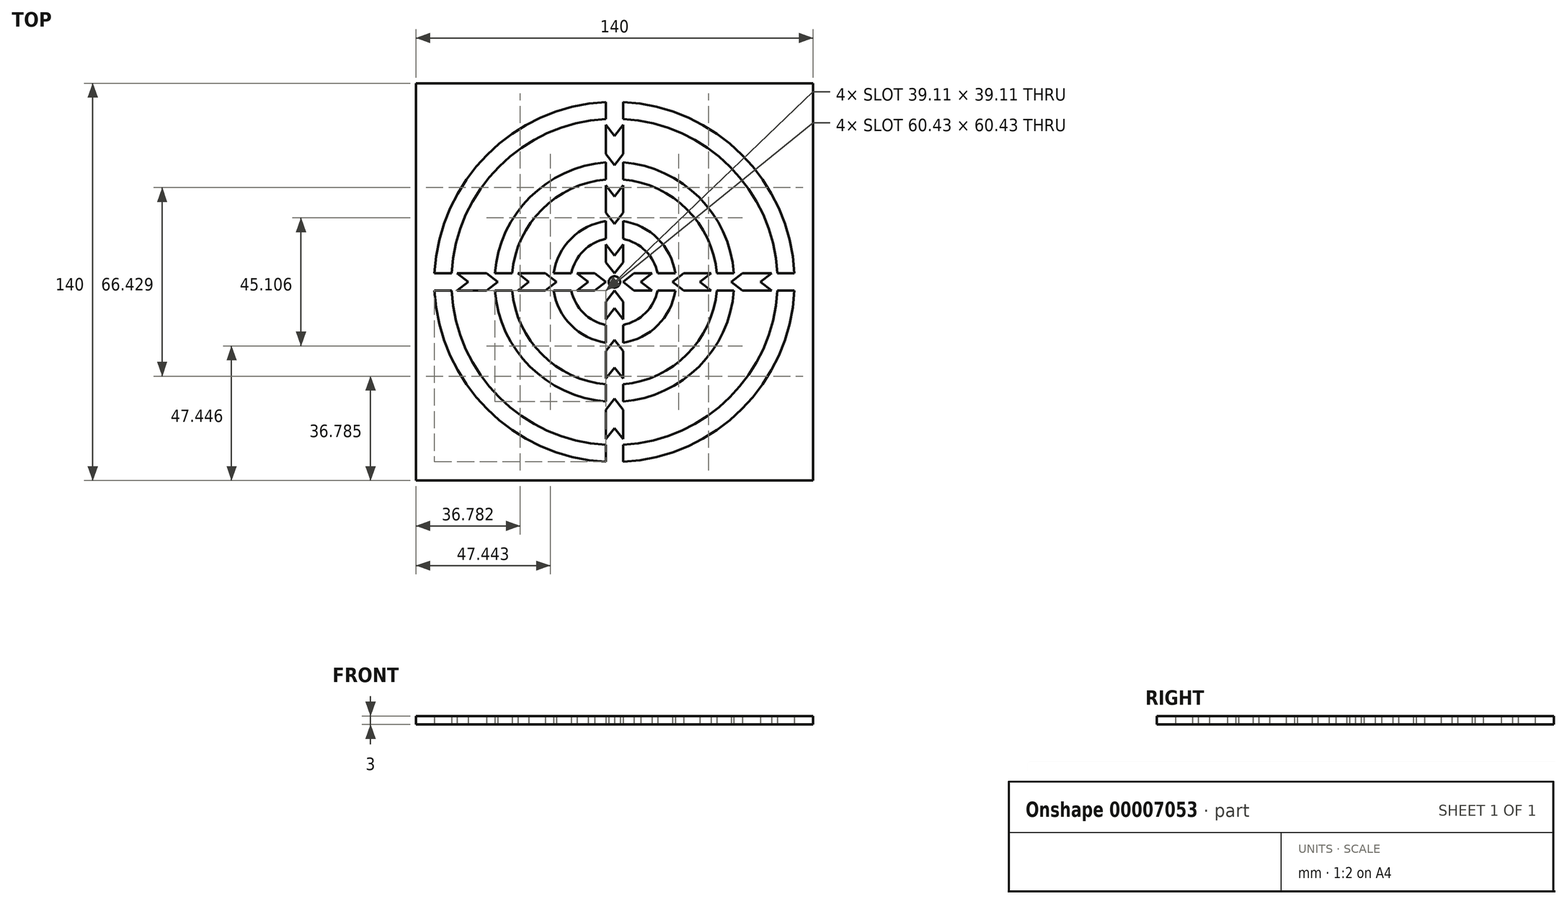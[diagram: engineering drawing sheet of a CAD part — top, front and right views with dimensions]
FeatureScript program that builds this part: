
annotation { "Feature Type Name" : "Feature", "Feature Type Description" : "" }
export const myFeature = defineFeature(function(context is Context, id is Id, definition is map)
    precondition{}
    {
        {
            var Q0;
            Q0=qCreatedBy(makeId("Top.planeOp"),FACE);
            var sketch = newSketch(context, id + "F0", { "sketchPlane" : qUnion([Q0])});
            skLineSegment(sketch, "E0.bottom", {"start": v(-138.4, 77.9) * mm, "end": v(1.6, 77.9) * mm});
            skLineSegment(sketch, "E0.top", {"start": v(-138.4, -62.1) * mm, "end": v(1.6, -62.1) * mm});
            skLineSegment(sketch, "E0.left", {"start": v(-138.4, 77.9) * mm, "end": v(-138.4, -62.1) * mm});
            skLineSegment(sketch, "E0.right", {"start": v(1.6, 77.9) * mm, "end": v(1.6, -62.1) * mm});
            skLineSegment(sketch, "E1", {"start": v(-138.4, 77.9) * mm, "end": v(1.6, -62.1) * mm, "construction": true});
            skLineSegment(sketch, "E2", {"start": v(1.6, 77.9) * mm, "end": v(-138.4, -62.1) * mm, "construction": true});
            skLineSegment(sketch, "E3", {"start": v(-68.4, 7.9) * mm, "end": v(-68.4, 77.9) * mm, "construction": true});
            skLineSegment(sketch, "E4", {"start": v(-68.4, 77.9) * mm, "end": v(-68.4, 7.9) * mm, "construction": true});
            skLineSegment(sketch, "E5", {"start": v(-68.4, 7.9) * mm, "end": v(1.6, 7.9) * mm, "construction": true});
            skLineSegment(sketch, "E6", {"start": v(1.6, 10.9) * mm, "end": v(-138.4, 10.9) * mm, "construction": true});
            skLineSegment(sketch, "E7", {"start": v(1.6, 4.9) * mm, "end": v(-138.4, 4.9) * mm, "construction": true});
            skLineSegment(sketch, "E8", {"start": v(-71.4, 77.9) * mm, "end": v(-71.4, -62.1) * mm, "construction": true});
            skLineSegment(sketch, "E9", {"start": v(-65.4, 77.9) * mm, "end": v(-65.4, -62.1) * mm, "construction": true});
            skLineSegment(sketch, "E10", {"start": v(-71.4, 71.33) * mm, "end": v(-71.4, 65.32) * mm});
            skLineSegment(sketch, "E11", {"start": v(-131.82, 10.9) * mm, "end": v(-125.82, 10.9) * mm});
            skArc(sketch, "E12", {"start": v(-71.4, 71.33) * mm, "mid": v(-113.26, 52.77) * mm, "end": v(-131.82, 10.9) * mm});
            skArc(sketch, "E13", {"start": v(-71.4, 65.32) * mm, "mid": v(-109.05, 48.55) * mm, "end": v(-125.82, 10.9) * mm});
            skArc(sketch, "E14", {"start": v(-71.4, 50) * mm, "mid": v(-98.21, 37.72) * mm, "end": v(-110.5, 10.9) * mm});
            skArc(sketch, "E15", {"start": v(-71.4, 43.99) * mm, "mid": v(-93.97, 33.48) * mm, "end": v(-104.48, 10.9) * mm});
            skLineSegment(sketch, "E16", {"start": v(-110.5, 10.9) * mm, "end": v(-104.48, 10.9) * mm});
            skLineSegment(sketch, "E17", {"start": v(-71.4, 50) * mm, "end": v(-71.4, 43.99) * mm});
            skLineSegment(sketch, "E18", {"start": v(-71.4, 29.31) * mm, "end": v(-71.4, 23.09) * mm});
            skLineSegment(sketch, "E19", {"start": v(-89.8, 10.9) * mm, "end": v(-83.58, 10.9) * mm});
            skArc(sketch, "E20", {"start": v(-71.4, 29.31) * mm, "mid": v(-83.68, 23.18) * mm, "end": v(-89.8, 10.9) * mm});
            skArc(sketch, "E21", {"start": v(-71.4, 23.09) * mm, "mid": v(-79.32, 18.83) * mm, "end": v(-83.58, 10.9) * mm});
            skLineSegment(sketch, "E22", {"start": v(-71.4, 63.32) * mm, "end": v(-68.4, 59.4) * mm});
            skLineSegment(sketch, "E23", {"start": v(-71.4, 53) * mm, "end": v(-68.4, 49.08) * mm});
            skLineSegment(sketch, "E24", {"start": v(-71.4, 32.31) * mm, "end": v(-68.4, 28.4) * mm});
            skLineSegment(sketch, "E25", {"start": v(-71.4, 21.09) * mm, "end": v(-68.4, 17.17) * mm});
            skLineSegment(sketch, "E26", {"start": v(-71.4, 14.82) * mm, "end": v(-68.4, 10.9) * mm});
            skLineSegment(sketch, "E27", {"start": v(-71.4, 41.99) * mm, "end": v(-68.4, 38.06) * mm});
            skLineSegment(sketch, "E28.MirrorCS", {"start": v(-123.82, 10.9) * mm, "end": v(-119.9, 7.9) * mm});
            skLineSegment(sketch, "E29.MirrorCS", {"start": v(-113.5, 10.9) * mm, "end": v(-109.58, 7.9) * mm});
            skLineSegment(sketch, "E30.MirrorCS", {"start": v(-102.48, 10.9) * mm, "end": v(-98.56, 7.9) * mm});
            skLineSegment(sketch, "E31.MirrorCS", {"start": v(-92.8, 10.9) * mm, "end": v(-88.89, 7.9) * mm});
            skLineSegment(sketch, "E32.MirrorCS", {"start": v(-75.32, 10.9) * mm, "end": v(-71.4, 7.9) * mm});
            skLineSegment(sketch, "E33.MirrorCS", {"start": v(-81.58, 10.9) * mm, "end": v(-77.66, 7.9) * mm});
            skLineSegment(sketch, "E34", {"start": v(-71.4, 63.32) * mm, "end": v(-71.4, 53) * mm});
            skLineSegment(sketch, "E35", {"start": v(-71.4, 41.99) * mm, "end": v(-71.4, 32.31) * mm});
            skLineSegment(sketch, "E36", {"start": v(-71.4, 21.09) * mm, "end": v(-71.4, 14.82) * mm});
            skLineSegment(sketch, "E37.MirrorCS", {"start": v(-123.82, 10.9) * mm, "end": v(-113.5, 10.9) * mm});
            skLineSegment(sketch, "E38.MirrorCS", {"start": v(-81.58, 10.9) * mm, "end": v(-75.32, 10.9) * mm});
            skLineSegment(sketch, "E39.MirrorCS", {"start": v(-102.48, 10.9) * mm, "end": v(-92.8, 10.9) * mm});
            skLineSegment(sketch, "E40.MirrorCS", {"start": v(-61.47, 10.9) * mm, "end": v(-65.4, 7.9) * mm});
            skLineSegment(sketch, "E41.MirrorCS", {"start": v(-55.2, 10.9) * mm, "end": v(-61.47, 10.9) * mm});
            skLineSegment(sketch, "E42.MirrorCS", {"start": v(-55.2, 10.9) * mm, "end": v(-59.12, 7.9) * mm});
            skLineSegment(sketch, "E43.MirrorCS", {"start": v(-46.98, 10.9) * mm, "end": v(-53.2, 10.9) * mm});
            skLineSegment(sketch, "E44.MirrorCS", {"start": v(-43.98, 10.9) * mm, "end": v(-47.9, 7.9) * mm});
            skLineSegment(sketch, "E45.MirrorCS", {"start": v(-34.3, 10.9) * mm, "end": v(-43.98, 10.9) * mm});
            skLineSegment(sketch, "E46.MirrorCS", {"start": v(-34.3, 10.9) * mm, "end": v(-38.23, 7.9) * mm});
            skLineSegment(sketch, "E47.MirrorCS", {"start": v(-26.29, 10.9) * mm, "end": v(-32.3, 10.9) * mm});
            skLineSegment(sketch, "E48.MirrorCS", {"start": v(-23.29, 10.9) * mm, "end": v(-27.2, 7.9) * mm});
            skLineSegment(sketch, "E49.MirrorCS", {"start": v(-12.97, 10.9) * mm, "end": v(-16.9, 7.9) * mm});
            skLineSegment(sketch, "E50.MirrorCS", {"start": v(-12.97, 10.9) * mm, "end": v(-23.29, 10.9) * mm});
            skLineSegment(sketch, "E51.MirrorCS", {"start": v(-4.96, 10.9) * mm, "end": v(-10.97, 10.9) * mm});
            skLineSegment(sketch, "E52.MirrorCS", {"start": v(-65.4, 14.82) * mm, "end": v(-68.4, 10.9) * mm});
            skArc(sketch, "E53.MirrorCS", {"start": v(-65.4, 23.09) * mm, "mid": v(-57.47, 18.83) * mm, "end": v(-53.2, 10.9) * mm});
            skLineSegment(sketch, "E54.MirrorCS", {"start": v(-65.4, 21.09) * mm, "end": v(-68.4, 17.17) * mm});
            skLineSegment(sketch, "E55.MirrorCS", {"start": v(-65.4, 29.31) * mm, "end": v(-65.4, 23.09) * mm});
            skArc(sketch, "E56.MirrorCS", {"start": v(-65.4, 29.31) * mm, "mid": v(-53.1, 23.18) * mm, "end": v(-46.98, 10.9) * mm});
            skLineSegment(sketch, "E57.MirrorCS", {"start": v(-65.4, 32.31) * mm, "end": v(-68.4, 28.4) * mm});
            skLineSegment(sketch, "E58.MirrorCS", {"start": v(-65.4, 41.99) * mm, "end": v(-68.4, 38.06) * mm});
            skLineSegment(sketch, "E59.MirrorCS", {"start": v(-65.4, 41.99) * mm, "end": v(-65.4, 32.31) * mm});
            skArc(sketch, "E60.MirrorCS", {"start": v(-65.4, 43.99) * mm, "mid": v(-42.82, 33.48) * mm, "end": v(-32.3, 10.9) * mm});
            skLineSegment(sketch, "E61.MirrorCS", {"start": v(-65.4, 50) * mm, "end": v(-65.4, 43.99) * mm});
            skArc(sketch, "E62.MirrorCS", {"start": v(-65.4, 50) * mm, "mid": v(-38.58, 37.72) * mm, "end": v(-26.29, 10.9) * mm});
            skLineSegment(sketch, "E63.MirrorCS", {"start": v(-65.4, 53) * mm, "end": v(-68.4, 49.08) * mm});
            skLineSegment(sketch, "E64.MirrorCS", {"start": v(-65.4, 63.32) * mm, "end": v(-65.4, 53) * mm});
            skLineSegment(sketch, "E65.MirrorCS", {"start": v(-65.4, 71.33) * mm, "end": v(-65.4, 65.32) * mm});
            skLineSegment(sketch, "E66.MirrorCS", {"start": v(-65.4, 63.32) * mm, "end": v(-68.4, 59.4) * mm});
            skArc(sketch, "E67.MirrorCS", {"start": v(-65.4, 65.32) * mm, "mid": v(-27.74, 48.55) * mm, "end": v(-10.97, 10.9) * mm});
            skArc(sketch, "E68.MirrorCS", {"start": v(-65.4, 71.33) * mm, "mid": v(-23.52, 52.77) * mm, "end": v(-4.96, 10.9) * mm});
            skLineSegment(sketch, "E69", {"start": v(-65.4, 21.09) * mm, "end": v(-65.4, 14.82) * mm});
            skLineSegment(sketch, "E70.MirrorCS", {"start": v(-4.96, 4.9) * mm, "end": v(-10.97, 4.9) * mm});
            skLineSegment(sketch, "E71.MirrorCS", {"start": v(-12.97, 4.9) * mm, "end": v(-16.9, 7.9) * mm});
            skLineSegment(sketch, "E72.MirrorCS", {"start": v(-12.97, 4.9) * mm, "end": v(-23.29, 4.9) * mm});
            skLineSegment(sketch, "E73.MirrorCS", {"start": v(-23.29, 4.9) * mm, "end": v(-27.2, 7.9) * mm});
            skLineSegment(sketch, "E74.MirrorCS", {"start": v(-26.29, 4.9) * mm, "end": v(-32.3, 4.9) * mm});
            skLineSegment(sketch, "E75.MirrorCS", {"start": v(-34.3, 4.9) * mm, "end": v(-38.23, 7.9) * mm});
            skLineSegment(sketch, "E76.MirrorCS", {"start": v(-34.3, 4.9) * mm, "end": v(-43.98, 4.9) * mm});
            skLineSegment(sketch, "E77.MirrorCS", {"start": v(-43.98, 4.9) * mm, "end": v(-47.9, 7.9) * mm});
            skLineSegment(sketch, "E78.MirrorCS", {"start": v(-46.98, 4.9) * mm, "end": v(-53.2, 4.9) * mm});
            skLineSegment(sketch, "E79.MirrorCS", {"start": v(-55.2, 4.9) * mm, "end": v(-59.12, 7.9) * mm});
            skLineSegment(sketch, "E80.MirrorCS", {"start": v(-55.2, 4.9) * mm, "end": v(-61.47, 4.9) * mm});
            skLineSegment(sketch, "E81.MirrorCS", {"start": v(-61.47, 4.9) * mm, "end": v(-65.4, 7.9) * mm});
            skLineSegment(sketch, "E82.MirrorCS", {"start": v(-131.82, 4.9) * mm, "end": v(-125.82, 4.9) * mm});
            skLineSegment(sketch, "E83.MirrorCS", {"start": v(-123.82, 4.9) * mm, "end": v(-119.9, 7.9) * mm});
            skLineSegment(sketch, "E84.MirrorCS", {"start": v(-123.82, 4.9) * mm, "end": v(-113.5, 4.9) * mm});
            skLineSegment(sketch, "E85.MirrorCS", {"start": v(-113.5, 4.9) * mm, "end": v(-109.58, 7.9) * mm});
            skLineSegment(sketch, "E86.MirrorCS", {"start": v(-110.5, 4.9) * mm, "end": v(-104.48, 4.9) * mm});
            skLineSegment(sketch, "E87.MirrorCS", {"start": v(-102.48, 4.9) * mm, "end": v(-98.56, 7.9) * mm});
            skLineSegment(sketch, "E88.MirrorCS", {"start": v(-102.48, 4.9) * mm, "end": v(-92.8, 4.9) * mm});
            skLineSegment(sketch, "E89.MirrorCS", {"start": v(-92.8, 4.9) * mm, "end": v(-88.89, 7.9) * mm});
            skLineSegment(sketch, "E90.MirrorCS", {"start": v(-75.32, 4.9) * mm, "end": v(-71.4, 7.9) * mm});
            skLineSegment(sketch, "E91.MirrorCS", {"start": v(-81.58, 4.9) * mm, "end": v(-77.66, 7.9) * mm});
            skLineSegment(sketch, "E92.MirrorCS", {"start": v(-81.58, 4.9) * mm, "end": v(-75.32, 4.9) * mm});
            skLineSegment(sketch, "E93.MirrorCS", {"start": v(-89.8, 4.9) * mm, "end": v(-83.58, 4.9) * mm});
            skLineSegment(sketch, "E94.MirrorCS", {"start": v(-71.4, 0.98) * mm, "end": v(-68.4, 4.9) * mm});
            skLineSegment(sketch, "E95.MirrorCS", {"start": v(-65.4, 0.98) * mm, "end": v(-68.4, 4.9) * mm});
            skLineSegment(sketch, "E96.MirrorCS", {"start": v(-65.4, -5.3) * mm, "end": v(-65.4, 0.98) * mm});
            skLineSegment(sketch, "E97.MirrorCS", {"start": v(-71.4, -5.3) * mm, "end": v(-71.4, 0.98) * mm});
            skArc(sketch, "E98.MirrorCS", {"start": v(-71.4, -7.3) * mm, "mid": v(-79.32, -3.03) * mm, "end": v(-83.58, 4.9) * mm});
            skLineSegment(sketch, "E99.MirrorCS", {"start": v(-71.4, -13.52) * mm, "end": v(-71.4, -7.3) * mm});
            skArc(sketch, "E100.MirrorCS", {"start": v(-65.4, -7.3) * mm, "mid": v(-57.47, -3.03) * mm, "end": v(-53.2, 4.9) * mm});
            skLineSegment(sketch, "E101.MirrorCS", {"start": v(-65.4, -13.52) * mm, "end": v(-65.4, -7.3) * mm});
            skLineSegment(sketch, "E102.MirrorCS", {"start": v(-65.4, -5.3) * mm, "end": v(-68.4, -1.37) * mm});
            skLineSegment(sketch, "E103.MirrorCS", {"start": v(-71.4, -5.3) * mm, "end": v(-68.4, -1.37) * mm});
            skArc(sketch, "E104.MirrorCS", {"start": v(-65.4, -13.52) * mm, "mid": v(-53.1, -7.38) * mm, "end": v(-46.98, 4.9) * mm});
            skArc(sketch, "E105.MirrorCS", {"start": v(-71.4, -13.52) * mm, "mid": v(-83.68, -7.38) * mm, "end": v(-89.8, 4.9) * mm});
            skLineSegment(sketch, "E106.MirrorCS", {"start": v(-71.4, -16.52) * mm, "end": v(-68.4, -12.6) * mm});
            skLineSegment(sketch, "E107.MirrorCS", {"start": v(-65.4, -16.52) * mm, "end": v(-68.4, -12.6) * mm});
            skLineSegment(sketch, "E108.MirrorCS", {"start": v(-65.4, -26.19) * mm, "end": v(-65.4, -16.52) * mm});
            skLineSegment(sketch, "E109.MirrorCS", {"start": v(-65.4, -26.19) * mm, "end": v(-68.4, -22.27) * mm});
            skLineSegment(sketch, "E110.MirrorCS", {"start": v(-71.4, -26.19) * mm, "end": v(-71.4, -16.52) * mm});
            skLineSegment(sketch, "E111.MirrorCS", {"start": v(-71.4, -26.19) * mm, "end": v(-68.4, -22.27) * mm});
            skArc(sketch, "E112.MirrorCS", {"start": v(-65.4, -28.19) * mm, "mid": v(-42.82, -17.68) * mm, "end": v(-32.3, 4.9) * mm});
            skArc(sketch, "E113.MirrorCS", {"start": v(-65.4, -34.2) * mm, "mid": v(-38.58, -21.92) * mm, "end": v(-26.29, 4.9) * mm});
            skLineSegment(sketch, "E114.MirrorCS", {"start": v(-65.4, -34.2) * mm, "end": v(-65.4, -28.19) * mm});
            skLineSegment(sketch, "E115.MirrorCS", {"start": v(-71.4, -34.2) * mm, "end": v(-71.4, -28.19) * mm});
            skArc(sketch, "E116.MirrorCS", {"start": v(-71.4, -28.19) * mm, "mid": v(-93.97, -17.68) * mm, "end": v(-104.48, 4.9) * mm});
            skArc(sketch, "E117.MirrorCS", {"start": v(-71.4, -34.2) * mm, "mid": v(-98.21, -21.92) * mm, "end": v(-110.5, 4.9) * mm});
            skLineSegment(sketch, "E118.MirrorCS", {"start": v(-71.4, -37.2) * mm, "end": v(-68.4, -33.29) * mm});
            skLineSegment(sketch, "E119.MirrorCS", {"start": v(-65.4, -37.2) * mm, "end": v(-68.4, -33.29) * mm});
            skLineSegment(sketch, "E120.MirrorCS", {"start": v(-65.4, -47.52) * mm, "end": v(-65.4, -37.2) * mm});
            skLineSegment(sketch, "E121.MirrorCS", {"start": v(-65.4, -47.52) * mm, "end": v(-68.4, -43.6) * mm});
            skLineSegment(sketch, "E122.MirrorCS", {"start": v(-71.4, -47.52) * mm, "end": v(-71.4, -37.2) * mm});
            skLineSegment(sketch, "E123.MirrorCS", {"start": v(-71.4, -47.52) * mm, "end": v(-68.4, -43.6) * mm});
            skArc(sketch, "E124.MirrorCS", {"start": v(-71.4, -49.52) * mm, "mid": v(-109.05, -32.76) * mm, "end": v(-125.82, 4.9) * mm});
            skArc(sketch, "E125.MirrorCS", {"start": v(-65.4, -49.52) * mm, "mid": v(-27.74, -32.76) * mm, "end": v(-10.97, 4.9) * mm});
            skArc(sketch, "E126.MirrorCS", {"start": v(-65.4, -55.53) * mm, "mid": v(-23.52, -36.97) * mm, "end": v(-4.96, 4.9) * mm});
            skLineSegment(sketch, "E127.MirrorCS", {"start": v(-71.4, -55.53) * mm, "end": v(-71.4, -49.52) * mm});
            skLineSegment(sketch, "E128.MirrorCS", {"start": v(-65.4, -55.53) * mm, "end": v(-65.4, -49.52) * mm});
            skArc(sketch, "E129.MirrorCS", {"start": v(-71.4, -55.53) * mm, "mid": v(-113.26, -36.97) * mm, "end": v(-131.82, 4.9) * mm});
            skCircle(sketch, "E130", {"center": v(-68.4, 7.9) * mm, "radius": 2 * mm});
            skSolve(sketch);
        }
        {
            var Q0;
            Q0=makeQuery(id+"F0.imprint","IMPRINT",FACE,{"disambiguationData":[TD([[makeQuery(id+"F0.imprint","IMPRINT",EDGE,{"derivedFrom":sQuery(id+"F0.wireOp",EDGE,"E0.bottom")}),-1.0]])]});
            extrude(context, id + "F1", {"entities" : qUnion([Q0]), "depth" : 3 * mm});
        }
    });
